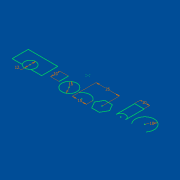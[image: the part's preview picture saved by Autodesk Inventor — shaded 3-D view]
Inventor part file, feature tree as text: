
AUTODESK INVENTOR PART (.ipt)
format: ipt  version: 2016 (Build 200138000, 138)  size: 73,216 bytes
history: native  units: mm
features: sketch x1
ambient origin geometry x8: Origin, YZ Plane, XZ Plane, XY Plane, X Axis, Y Axis, Z Axis, Center Point
feature tree (1):
  sketch  "Sketch1"  dims[d0=15.0mm d4=16.0mm d8=10.0mm d10=25.0mm d14=10.0mm d16=10.0mm d18=12.0mm]
